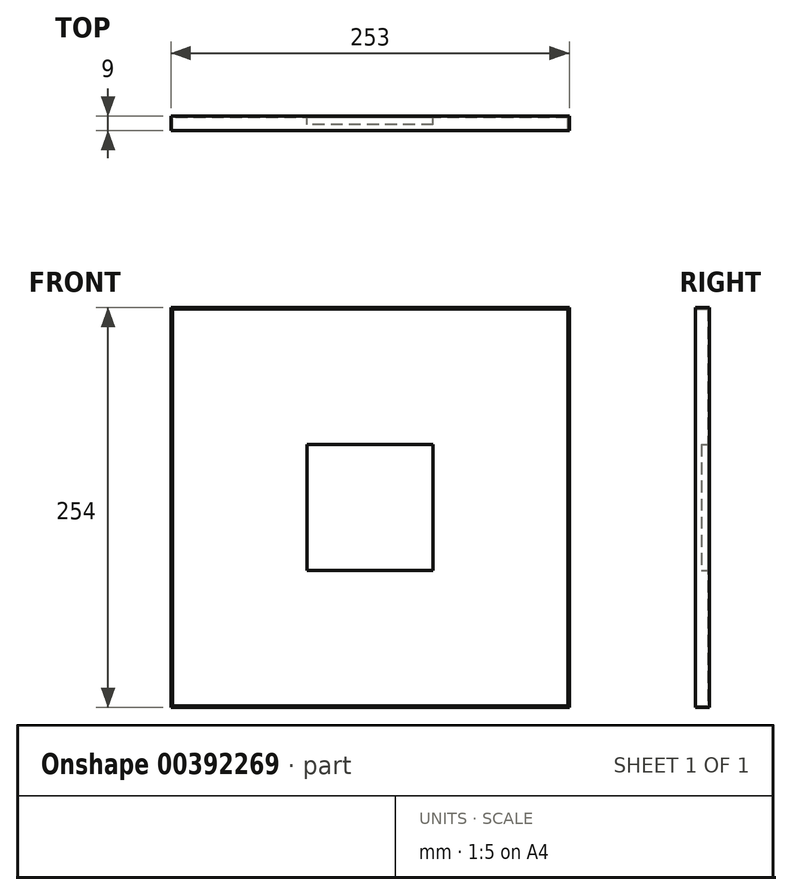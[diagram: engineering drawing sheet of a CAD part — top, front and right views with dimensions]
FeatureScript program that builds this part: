
annotation { "Feature Type Name" : "Feature", "Feature Type Description" : "" }
export const myFeature = defineFeature(function(context is Context, id is Id, definition is map)
    precondition{}
    {
        {
            var Q0;
            Q0=qCreatedBy(makeId("Front.planeOp"),FACE);
            var sketch = newSketch(context, id + "F0", { "sketchPlane" : qUnion([Q0])});
            skLineSegment(sketch, "E0.bottom", {"start": v(126.5, 127) * mm, "end": v(-126.5, 127) * mm});
            skLineSegment(sketch, "E0.top", {"start": v(126.5, -127) * mm, "end": v(-126.5, -127) * mm});
            skLineSegment(sketch, "E0.left", {"start": v(126.5, 127) * mm, "end": v(126.5, -127) * mm});
            skLineSegment(sketch, "E0.right", {"start": v(-126.5, 127) * mm, "end": v(-126.5, -127) * mm});
            skPoint(sketch, "E0.middle", {"position": v(0, 0) * mm});
            skSolve(sketch);
        }
        {
            var Q0;
            Q0 = qSketchRegion(id + "F0", true);
            extrude(context, id + "F1", {"entities" : qUnion([Q0]), "depth" : 1 * mm});
        }
        {
            var Q0;
            Q0=makeQuery(id+"F1.opExtrude","CAP_FACE",FACE,{"disambiguationData":[OSD([sQuery(id+"F0.wireOp",EDGE,"E0.bottom"),sQuery(id+"F0.wireOp",EDGE,"E0.top"),sQuery(id+"F0.wireOp",EDGE,"E0.left"),sQuery(id+"F0.wireOp",EDGE,"E0.right")])],"isStart":false});
            var sketch = newSketch(context, id + "F2", { "sketchPlane" : qUnion([Q0])});
            skLineSegment(sketch, "E1.bottom", {"start": v(125.5, 126) * mm, "end": v(-125.5, 126) * mm});
            skLineSegment(sketch, "E1.top", {"start": v(125.5, -126) * mm, "end": v(-125.5, -126) * mm});
            skLineSegment(sketch, "E1.left", {"start": v(125.5, 126) * mm, "end": v(125.5, -126) * mm});
            skLineSegment(sketch, "E1.right", {"start": v(-125.5, 126) * mm, "end": v(-125.5, -126) * mm});
            skPoint(sketch, "E1.middle", {"position": v(0, 0) * mm});
            skLineSegment(sketch, "E2.bottom", {"start": v(126.5, 127) * mm, "end": v(-126.5, 127) * mm});
            skLineSegment(sketch, "E2.top", {"start": v(126.5, -127) * mm, "end": v(-126.5, -127) * mm});
            skLineSegment(sketch, "E2.left", {"start": v(126.5, 127) * mm, "end": v(126.5, -127) * mm});
            skLineSegment(sketch, "E2.right", {"start": v(-126.5, 127) * mm, "end": v(-126.5, -127) * mm});
            skSolve(sketch);
        }
        {
            var Q0;
            Q0 = qSketchRegion(id + "F2", true);
            extrude(context, id + "F3", {"entities" : qUnion([Q0]), "operationType" : NewBodyOperationType.ADD, "depth" : 8 * mm});
        }
        {
            var Q0;
            Q0=makeQuery(id+"F1.opExtrude","CAP_FACE",FACE,{"disambiguationData":[OSD([sQuery(id+"F0.wireOp",EDGE,"E0.bottom"),sQuery(id+"F0.wireOp",EDGE,"E0.top"),sQuery(id+"F0.wireOp",EDGE,"E0.left"),sQuery(id+"F0.wireOp",EDGE,"E0.right")])],"isStart":false});
            var sketch = newSketch(context, id + "F4", { "sketchPlane" : qUnion([Q0])});
            skLineSegment(sketch, "E3.bottom", {"start": v(40, 40) * mm, "end": v(-40, 40) * mm});
            skLineSegment(sketch, "E3.top", {"start": v(40, -40) * mm, "end": v(-40, -40) * mm});
            skLineSegment(sketch, "E3.left", {"start": v(40, 40) * mm, "end": v(40, -40) * mm});
            skLineSegment(sketch, "E3.right", {"start": v(-40, 40) * mm, "end": v(-40, -40) * mm});
            skPoint(sketch, "E3.middle", {"position": v(0, 0) * mm});
            skSolve(sketch);
        }
        {
            var Q0;
            Q0 = qSketchRegion(id + "F4", true);
            extrude(context, id + "F5", {"entities" : qUnion([Q0]), "operationType" : NewBodyOperationType.ADD, "depth" : 4.2 * mm});
        }
    });
